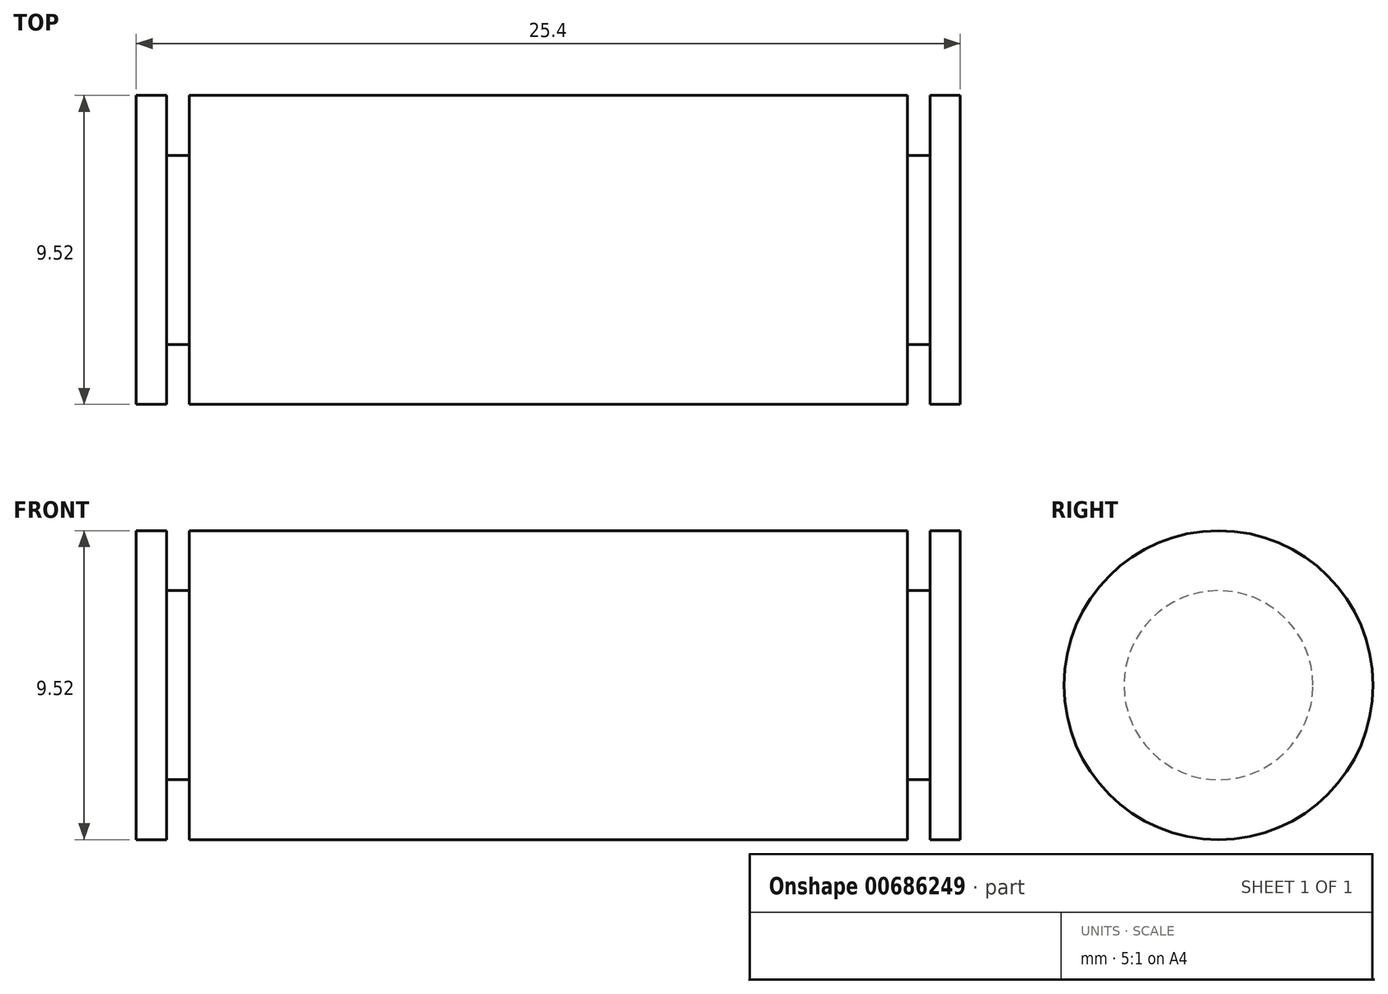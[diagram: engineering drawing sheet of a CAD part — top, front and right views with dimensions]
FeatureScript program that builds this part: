
annotation { "Feature Type Name" : "Feature", "Feature Type Description" : "" }
export const myFeature = defineFeature(function(context is Context, id is Id, definition is map)
    precondition{}
    {
        {
            var Q0;
            Q0=qCreatedBy(makeId("Right.planeOp"),FACE);
            var sketch = newSketch(context, id + "F0", { "sketchPlane" : qUnion([Q0])});
            skCircle(sketch, "E0", {"center": v(0, 0) * mm, "radius": 4.76 * mm});
            skSolve(sketch);
        }
        {
            var Q0;
            Q0 = qSketchRegion(id + "F0", true);
            extrude(context, id + "F1", {"entities" : qUnion([Q0]), "depth" : 12.7 * mm, "offsetDistance" : 25.4 * mm});
        }
        {
            var Q0;
            Q0=qCreatedBy(makeId("Top.planeOp"),FACE);
            var sketch = newSketch(context, id + "F2", { "sketchPlane" : qUnion([Q0])});
            skLineSegment(sketch, "E1.bottom", {"start": v(11.77, 5.2) * mm, "end": v(11.07, 5.2) * mm});
            skLineSegment(sketch, "E1.top", {"start": v(11.77, 2.91) * mm, "end": v(11.07, 2.91) * mm});
            skLineSegment(sketch, "E1.left", {"start": v(11.77, 5.2) * mm, "end": v(11.77, 2.91) * mm});
            skLineSegment(sketch, "E1.right", {"start": v(11.07, 5.2) * mm, "end": v(11.07, 2.91) * mm});
            skLineSegment(sketch, "E2", {"start": v(15.49, 0) * mm, "end": v(7.73, 0) * mm, "construction": true});
            skSolve(sketch);
        }
        {
            var Q0;
            Q0 = qSketchRegion(id + "F2", true);
            var Q1;
            Q1=sQuery(id+"F2.wireOp",EDGE,"E2");
            revolve(context, id + "F3", {"operationType" : NewBodyOperationType.REMOVE, "surfaceOperationType" : NewSurfaceOperationType.NEW, "entities" : qUnion([Q0]), "axis" : qUnion([Q1]), "revolveType" : RevolveType.FULL, "oppositeDirection" : true});
        }
        {
            var Q0;
            Q0=makeQuery(id+"F1.opExtrude","SWEPT_BODY",BODY,{"disambiguationData":[OSD([sQuery(id+"F0.wireOp",EDGE,"E0")])]});
            var Q1;
            Q1=qCreatedBy(makeId("Right.planeOp"),FACE);
            mirror(context, id + "F4", {"operationType" : NewBodyOperationType.ADD, "entities" : qUnion([Q0]), "mirrorPlane" : qUnion([Q1])});
        }
    });
